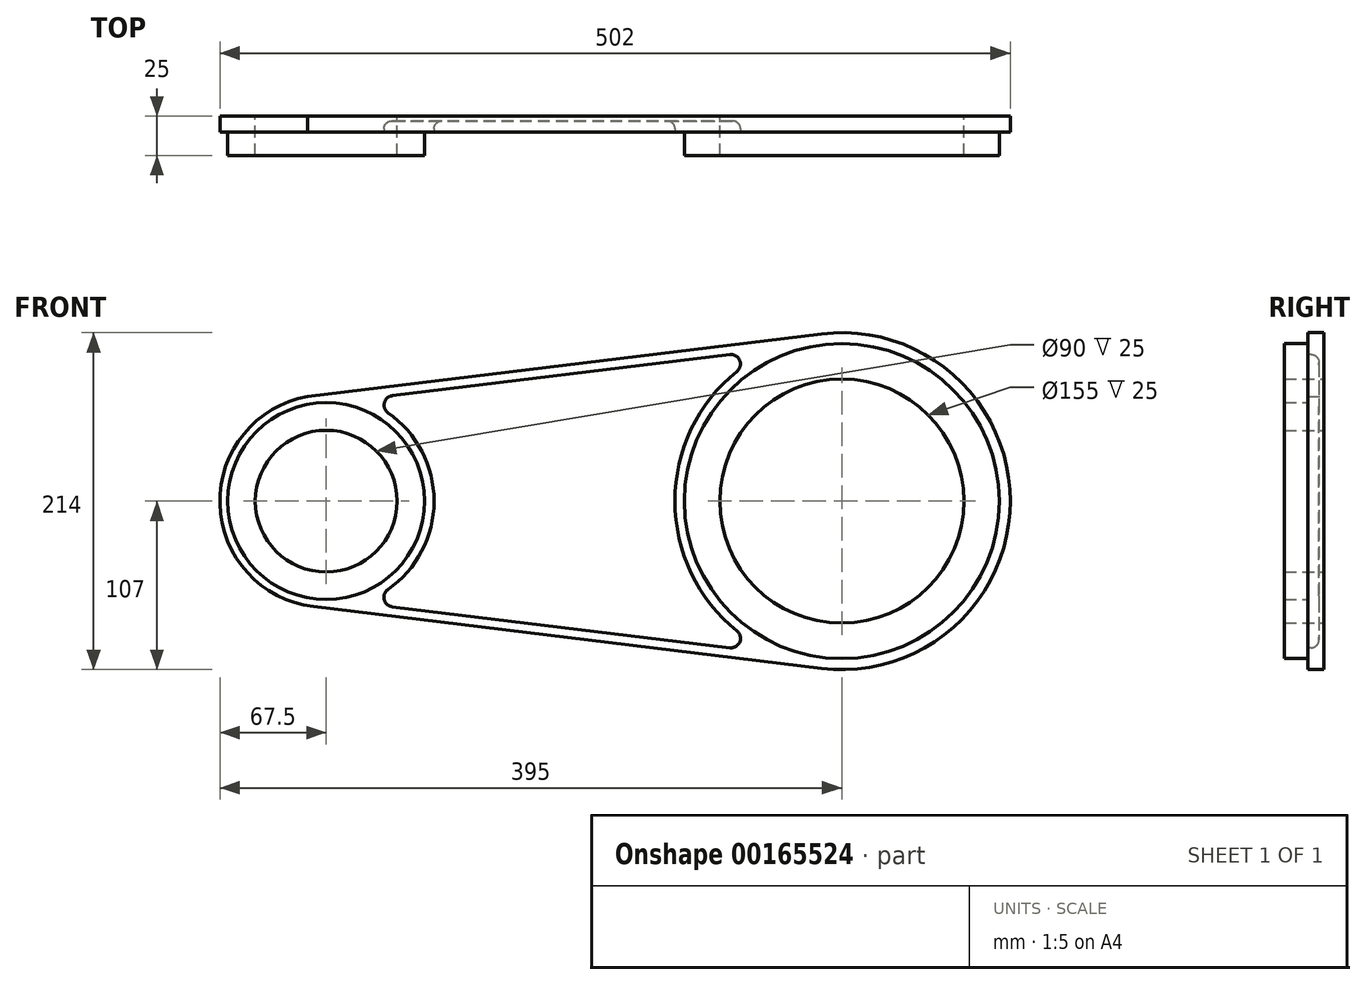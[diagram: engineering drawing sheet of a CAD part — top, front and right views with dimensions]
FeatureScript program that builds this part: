
annotation { "Feature Type Name" : "Feature", "Feature Type Description" : "" }
export const myFeature = defineFeature(function(context is Context, id is Id, definition is map)
    precondition{}
    {
        {
            var Q0;
            Q0=qCreatedBy(makeId("Front.planeOp"),FACE);
            var sketch = newSketch(context, id + "F0", { "sketchPlane" : qUnion([Q0])});
            skCircle(sketch, "E0", {"center": v(0, 0) * mm, "radius": 100 * mm});
            skCircle(sketch, "E1", {"center": v(-327.5, 0) * mm, "radius": 62.5 * mm});
            skArc(sketch, "E2", {"start": v(-12.9, -106.22) * mm, "mid": v(107, 0.02) * mm, "end": v(-12.94, 106.22) * mm});
            skArc(sketch, "E3", {"start": v(-339.2, 66.48) * mm, "mid": v(-394.98, -1.8) * mm, "end": v(-335.64, -67) * mm});
            skLineSegment(sketch, "E4", {"start": v(-339.2, 66.48) * mm, "end": v(-12.94, 106.22) * mm});
            skLineSegment(sketch, "E5", {"start": v(-12.9, -106.22) * mm, "end": v(-335.64, -67) * mm});
            skSolve(sketch);
        }
        {
            var Q0;
            Q0=makeQuery(id+"F0.imprint","IMPRINT",FACE,{"disambiguationData":[TD([[makeQuery(id+"F0.imprint","IMPRINT",EDGE,{"derivedFrom":sQuery(id+"F0.wireOp",EDGE,"E0")}),-1.0]])]});
            extrude(context, id + "F1", {"entities" : qUnion([Q0]), "depth" : 10 * mm});
        }
        {
            var Q0;
            Q0=makeQuery(id+"F1.opExtrude","CAP_FACE",FACE,{"disambiguationData":[OSD([sQuery(id+"F0.wireOp",EDGE,"E0"),sQuery(id+"F0.wireOp",EDGE,"E1"),sQuery(id+"F0.wireOp",EDGE,"E2"),sQuery(id+"F0.wireOp",EDGE,"E3"),sQuery(id+"F0.wireOp",EDGE,"E4"),sQuery(id+"F0.wireOp",EDGE,"E5")])],"isStart":false});
            var sketch = newSketch(context, id + "F2", { "sketchPlane" : qUnion([Q0])});
            skCircle(sketch, "E6.0", {"center": v(-327.5, 0) * mm, "radius": 62.5 * mm});
            skCircle(sketch, "E7.0", {"center": v(0, 0) * mm, "radius": 100 * mm});
            skCircle(sketch, "E8", {"center": v(-327.5, 0) * mm, "radius": 45 * mm});
            skCircle(sketch, "E9", {"center": v(0, 0) * mm, "radius": 77.5 * mm});
            skSolve(sketch);
        }
        {
            var Q0;
            Q0=makeQuery(id+"F2.imprint","IMPRINT",FACE,{"disambiguationData":[TD([[makeQuery(id+"F2.imprint","IMPRINT",EDGE,{"derivedFrom":sQuery(id+"F2.wireOp",EDGE,"E6.0")}),1.0]])]});
            var Q1;
            Q1=makeQuery(id+"F2.imprint","IMPRINT",FACE,{"disambiguationData":[TD([[makeQuery(id+"F2.imprint","IMPRINT",EDGE,{"derivedFrom":sQuery(id+"F2.wireOp",EDGE,"E7.0")}),1.0]])]});
            extrude(context, id + "F3", {"entities" : qUnion([Q0, Q1]), "operationType" : NewBodyOperationType.ADD, "depth" : 15 * mm, "hasSecondDirection" : true, "secondDirectionOppositeDirection" : true, "secondDirectionDepth" : 10 * mm});
        }
        {
            var Q0;
            Q0=makeQuery(id+"F1.opExtrude","CAP_FACE",FACE,{"disambiguationData":[OSD([sQuery(id+"F0.wireOp",EDGE,"E0"),sQuery(id+"F0.wireOp",EDGE,"E1"),sQuery(id+"F0.wireOp",EDGE,"E2"),sQuery(id+"F0.wireOp",EDGE,"E3"),sQuery(id+"F0.wireOp",EDGE,"E4"),sQuery(id+"F0.wireOp",EDGE,"E5")])],"isStart":false});
            var sketch = newSketch(context, id + "F4", { "sketchPlane" : qUnion([Q0])});
            skArc(sketch, "E10.0", {"start": v(-66.6, 82.46) * mm, "mid": v(-106, -0.02) * mm, "end": v(-66.58, -82.48) * mm});
            skLineSegment(sketch, "E11.0", {"start": v(-285.58, -67.05) * mm, "end": v(-71.07, -93.1) * mm});
            skLineSegment(sketch, "E11.2", {"start": v(-71.1, 93.09) * mm, "end": v(-285.48, 66.98) * mm});
            skArc(sketch, "E12.0", {"start": v(-288.3, -56.17) * mm, "mid": v(-259, -0.06) * mm, "end": v(-288.2, 56.1) * mm});
            skPoint(sketch, "E13.visualSharp", {"position": v(-304.79, 64.63) * mm});
            skArc(sketch, "E13.filletArc", {"start": v(-285.48, 66.98) * mm, "mid": v(-290.58, 62.48) * mm, "end": v(-288.2, 56.1) * mm});
            skPoint(sketch, "E14.visualSharp", {"position": v(-44.15, 96.37) * mm});
            skArc(sketch, "E14.filletArc", {"start": v(-66.6, 82.46) * mm, "mid": v(-64.85, 89.47) * mm, "end": v(-71.1, 93.09) * mm});
            skPoint(sketch, "E15.visualSharp", {"position": v(-44.12, -96.38) * mm});
            skArc(sketch, "E15.filletArc", {"start": v(-71.07, -93.1) * mm, "mid": v(-64.82, -89.49) * mm, "end": v(-66.58, -82.48) * mm});
            skPoint(sketch, "E16.visualSharp", {"position": v(-304.97, -64.69) * mm});
            skArc(sketch, "E16.filletArc", {"start": v(-288.3, -56.17) * mm, "mid": v(-290.68, -62.54) * mm, "end": v(-285.58, -67.05) * mm});
            skSolve(sketch);
        }
        {
            var Q0;
            Q0=makeQuery(id+"F4.imprint","IMPRINT",FACE,{"disambiguationData":[TD([[makeQuery(id+"F4.imprint","IMPRINT",EDGE,{"derivedFrom":sQuery(id+"F4.wireOp",EDGE,"E10.0")}),-1.0]])]});
            extrude(context, id + "F5", {"entities" : qUnion([Q0]), "operationType" : NewBodyOperationType.REMOVE, "oppositeDirection" : true, "depth" : 7 * mm});
        }
        {
            var Q0;
            Q0=makeQuery(id+"F5.boolean.opBoolean","COPY",EDGE,{"derivedFrom":makeQuery(id+"F5.opExtrude","CAP_EDGE",EDGE,{"disambiguationData":[OSD([sQuery(id+"F4.wireOp",EDGE,"E10.0")])],"isStart":false})});
            fillet(context, id + "F6", {"entities" : qUnion([Q0]), "radius" : 5 * mm, "tangentPropagation" : true, "allowEdgeOverflow" : false});
        }
    });
